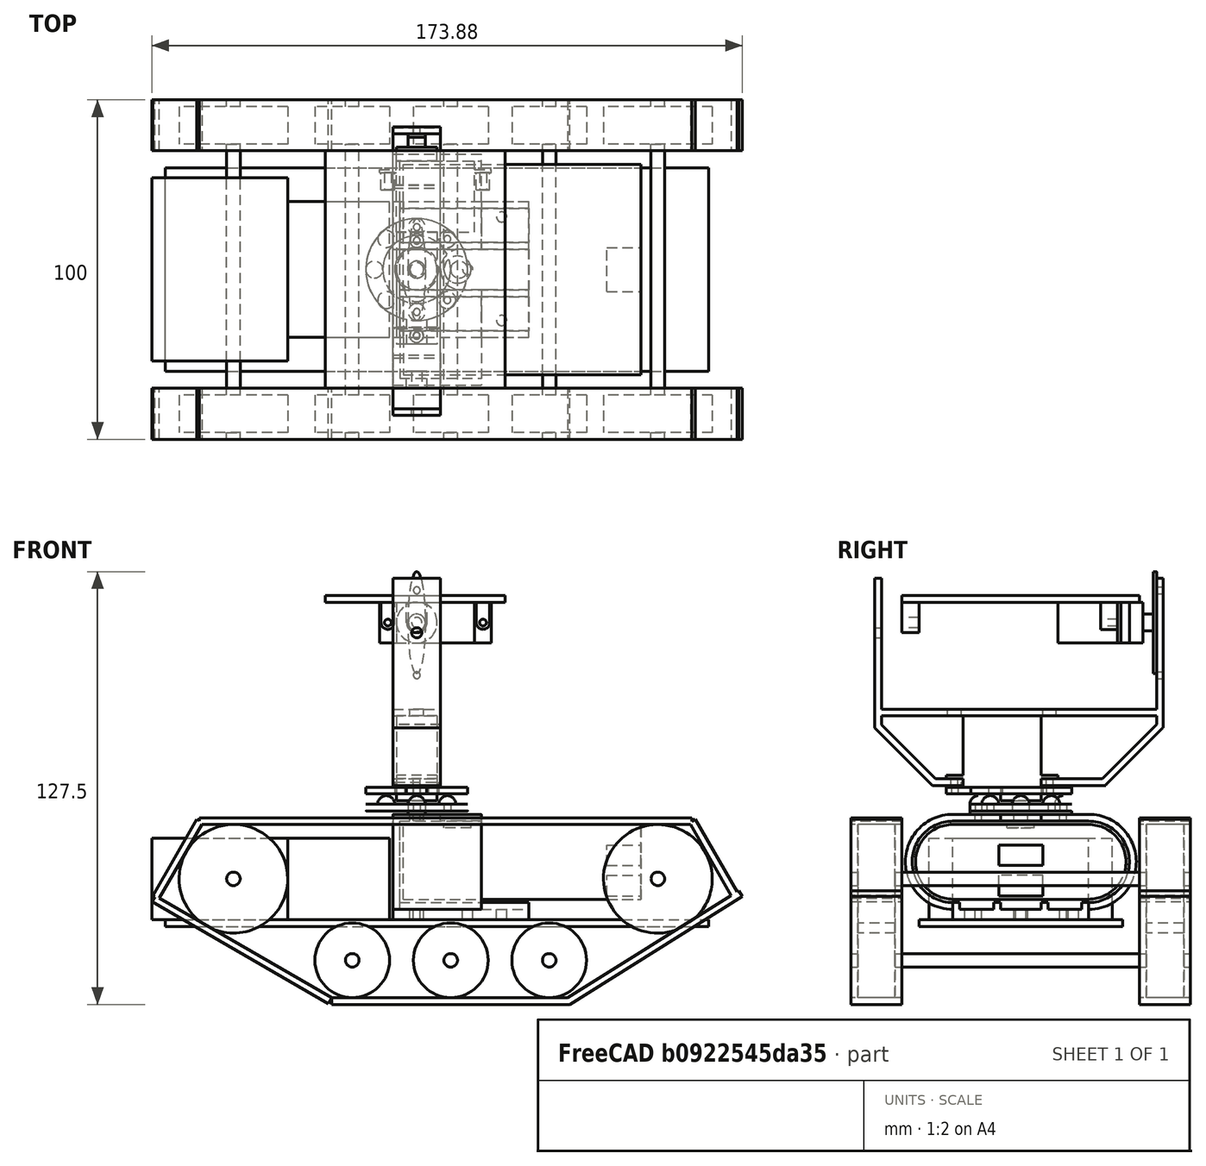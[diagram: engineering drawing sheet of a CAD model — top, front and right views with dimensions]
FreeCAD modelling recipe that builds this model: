
FCSTD DOCUMENT
Label: androidtank_6
License: CC-BY 3.0
LicenseURL: http://creativecommons.org/licenses/by/3.0/
objects: Part::Cylinder×51, Part::Box×36, Part::MultiFuse×25, Part::Sphere×8, Part::Cut×7, Part::FeaturePython×1, App::DocumentObjectGroup×1
note: 128 computed .brp shape members not serialized (recipe doc carries the construction recipe); baked Part::Feature solids carry a one-line shape summary decoded from their .brp

FEATURE [Part::Box] Box  label="MainFrame"
  Height = 2
  Length = 160
  Width = 60
FEATURE [Part::Box] Box001001  label="Moter Unit2"
  Height = 24
  Length = 30
  Placement = pos=(36,10,2) rot=(0,0,1;0rad)
  Width = 40
FEATURE [Part::Cylinder] Cylinder  label="Shaft"
  Angle = 360
  Height = 100
  Placement = pos=(20,-20,14) rot=(-1,0,0;1.5708rad)
  Radius = 2
FEATURE [Part::Box] Box001002
  Height = 2
  Length = 145
  Placement = pos=(10,-20,30) rot=(0,0,1;0rad)
  Width = 15
FEATURE [Part::Box] Box001002001
  Height = 2
  Length = 70
  Placement = pos=(49,-20,-23) rot=(0,0,1;0rad)
  Width = 15
FEATURE [Part::Box] Box001002001001
  Height = 2
  Length = 60
  Placement = pos=(119,-20,-23) rot=(0,-1,0;0.558505rad)
  Width = 15
FEATURE [Part::Box] Box001002001002
  Height = 2
  Length = 60
  Placement = pos=(49,-20,-21) rot=(0,1,0;3.66519rad)
  Width = 15
FEATURE [Part::Box] Box001002001003
  Height = 2
  Length = 26
  Placement = pos=(-2,-20,8) rot=(0,-1,0;1.0472rad)
  Width = 15
FEATURE [Part::Box] Box001002001003001
  Height = 2
  Length = 26
  Placement = pos=(169,-20,9) rot=(0,-1,0;2.0944rad)
  Width = 15
FEATURE [Part::MultiFuse] Fusion002001002  label="Caterpiller1"
  Shapes = -> [Box001002,Box001002001,Box001002001002,Box001002001001,Box001002001003,Box001002001003001]
FEATURE [Part::MultiFuse] Fusion002001002001  label="Caterpiller2"
  Placement = pos=(0,85,0) rot=(0,0,1;0rad)
  Shapes = -> [Box001002,Box001002001,Box001002001002,Box001002001001,Box001002001003,Box001002001003001]
FEATURE [Part::Cylinder] Cylinder002001001002  label="Wheel006"
  Angle = 360
  Height = 11
  Placement = pos=(20,78,14) rot=(1,0,0;1.5708rad)
  Radius = 11
FEATURE [Part::Cylinder] Cylinder002001001002001  label="Wheel007"
  Angle = 360
  Height = 11
  Placement = pos=(20,-7,14) rot=(1,0,0;1.5708rad)
  Radius = 11
FEATURE [Part::Cylinder] Cylinder002001002001  label="Shaft002"
  Angle = 360
  Height = 100
  Placement = pos=(20,-20,14) rot=(-1,0,0;1.5708rad)
  Radius = 2
FEATURE [Part::MultiFuse] Fusion002001002002002  label="SWheelSet1"
  Placement = pos=(35,0,-24) rot=(0,0,1;0rad)
  Shapes = -> [Cylinder002001002001,Cylinder002001001002,Cylinder002001001002001]
FEATURE [Part::MultiFuse] Fusion002001002002002001  label="SWheelSet2"
  Placement = pos=(64,0,-24) rot=(0,0,1;0rad)
  Shapes = -> [Cylinder002001002001,Cylinder002001001002,Cylinder002001001002001]
FEATURE [Part::MultiFuse] Fusion002001002002002001001  label="SWheelSet3"
  Placement = pos=(93,0,-24) rot=(0,0,1;0rad)
  Shapes = -> [Cylinder002001002001,Cylinder002001001002,Cylinder002001001002001]
FEATURE [Part::Box] Box001002001003002
  Height = 22
  Length = 70
  Placement = pos=(0,0,-11) rot=(0,0,1;0rad)
  Width = 40
FEATURE [Part::Cylinder] Cylinder002001001002002
  Angle = 360
  Height = 70
  Placement = pos=(0,0,0) rot=(0,1,0;1.5708rad)
  Radius = 11
FEATURE [Part::Cylinder] Cylinder001
  Angle = 360
  Height = 70
  Placement = pos=(0,40,0) rot=(0,1,0;1.5708rad)
  Radius = 11
FEATURE [Part::Cylinder] Cylinder002001001002003  label="PowerButton"
  Angle = 360
  Height = 2
  Placement = pos=(16,20,10) rot=(0,0,1;0rad)
  Radius = 4
FEATURE [Part::Box] Box001002001003003  label="USB1"
  Height = 6
  Length = 15
  Placement = pos=(60,13.5,-1) rot=(0,0,1;0rad)
  Width = 13
FEATURE [Part::Box] Box001001001  label="USB2"
  Height = 6
  Length = 15
  Placement = pos=(60,13.5,-10) rot=(0,0,1;0rad)
  Width = 13
FEATURE [Part::MultiFuse] Fusion002001002002002001002
  Shapes = -> [Cylinder001,Box001002001003002,Cylinder002001001002002]
FEATURE [Part::MultiFuse] Fusion001001
  Shapes = -> [Box001001001,Cylinder002001001002003,Box001002001003003]
FEATURE [Part::Cut] Cut  label="Eneloop"
  Base = -> Fusion002001002002002001002
  Placement = pos=(70,10,19) rot=(0,0,1;0rad)
  Tool = -> Fusion001001
FEATURE [Part::Cylinder] Cylinder001001  label="Cylinder002"
  Angle = 360
  Height = 26
  Placement = pos=(0,50,19) rot=(0,1,0;1.5708rad)
  Radius = 14
FEATURE [Part::Box] Box001002001003002001  label="Box001002001003002001001001001006001001002001003001006"
  Height = 28
  Length = 26
  Placement = pos=(0,10,5) rot=(0,0,1;0rad)
  Width = 40
FEATURE [Part::Cylinder] Cylinder002001001002002001  label="Cylinder003"
  Angle = 360
  Height = 26
  Placement = pos=(0,10,19) rot=(0,1,0;1.5708rad)
  Radius = 14
FEATURE [Part::Box] Box001  label="Moter Unit1"
  Height = 24
  Length = 40
  Placement = pos=(-4,3,2) rot=(0,0,1;0rad)
  Width = 54
FEATURE [Part::Box] Box001002001003002001001  label="Box003"
  Height = 5
  Length = 40
  Placement = pos=(0,10,2) rot=(0,0,1;0rad)
  Width = 40
FEATURE [Part::Box] Box001002001003002001002  label="Box004"
  Height = 24
  Length = 26
  Placement = pos=(2,10,7) rot=(0,0,1;0rad)
  Width = 40
FEATURE [Part::Cylinder] Cylinder001001001  label="Cylinder004"
  Angle = 360
  Height = 26
  Placement = pos=(2,50,19) rot=(0,1,0;1.5708rad)
  Radius = 12
FEATURE [Part::Cylinder] Cylinder002001001002002001001  label="Cylinder005"
  Angle = 360
  Height = 26
  Placement = pos=(2,10,19) rot=(0,1,0;1.5708rad)
  Radius = 12
FEATURE [Part::Cylinder] Cylinder002001001002003001  label="PowerButton001"
  Angle = 360
  Height = 4
  Placement = pos=(20,30,30) rot=(0,0,1;0rad)
  Radius = 6
FEATURE [Part::Box] Box001002001003002001003  label="Box005"
  Height = 4
  Length = 10
  Placement = pos=(20,24,30) rot=(0,0,1;0rad)
  Width = 12
FEATURE [Part::Box] Box001002001003002001001001  label="Box006"
  Height = 3
  Length = 40
  Placement = pos=(2,12,5) rot=(0,0,1;0rad)
  Width = 10
FEATURE [Part::Box] Box001002001003002001001001001  label="Box007"
  Height = 3
  Length = 40
  Placement = pos=(2,24,5) rot=(0,0,1;0rad)
  Width = 12
FEATURE [Part::Box] Box001002001003002001001001001001  label="Box008"
  Height = 3
  Length = 40
  Placement = pos=(2,38,5) rot=(0,0,1;0rad)
  Width = 10
FEATURE [Part::MultiFuse] Fusion002001002002002001003
  Shapes = -> [Box001002001003002001,Cylinder001001,Cylinder002001001002002001,Box001002001003002001001]
FEATURE [Part::MultiFuse] Fusion002001002002002001004
  Shapes = -> [Box001002001003002001002,Cylinder002001001002002001001,Cylinder001001001,Box001002001003002001001001001001,Box001002001003002001001001001,Box001002001003002001001001,Box001002001003002001003,Cylinder002001001002003001]
FEATURE [Part::Cut] Cut001  label="BatteryFrame"
  Base = -> Fusion002001002002002001003
  Placement = pos=(67,0,0) rot=(0,0,1;0rad)
  Tool = -> Fusion002001002002002001004
FEATURE [Part::Cylinder] Cylinder002001001002002001002001  label="Cylinder007"
  Angle = 360
  Height = 40
  Placement = pos=(74,17.5,0) rot=(0,0,1;0rad)
  Radius = 1
FEATURE [Part::Cylinder] Cylinder002001001002002001002  label="Cylinder006"
  Angle = 360
  Height = 40
  Placement = pos=(74,42.5,0) rot=(0,0,1;0rad)
  Radius = 1
FEATURE [Part::Cylinder] Cylinder002001001002002001002001001  label="Cylinder008"
  Angle = 360
  Height = 40
  Placement = pos=(89,30,0) rot=(0,0,1;0rad)
  Radius = 1.5
FEATURE [Part::Cylinder] Cylinder002001001002002001002001002  label="Cylinder009"
  Angle = 360
  Height = 40
  Placement = pos=(99,45.5,0) rot=(0,0,1;0rad)
  Radius = 1.5
FEATURE [Part::Cylinder] Cylinder002001001002002001002001003  label="Cylinder0010"
  Angle = 360
  Height = 40
  Placement = pos=(99,15,0) rot=(0,0,1;0rad)
  Radius = 1.5
FEATURE [Part::Box] Box001002001003002001001001001006  label="Box009"
  Height = 2
  Length = 53
  Placement = pos=(47,-5,100) rot=(0,0,1;0rad)
  Width = 70
FEATURE [Part::Box] Box001002001003002001001001001006001  label="Box010"
  Height = 44
  Length = 14
  Placement = pos=(67,70,66) rot=(0,0,1;0rad)
  Width = 2
FEATURE [Part::Box] Box001002001003002001001001001006001001  label="Box011"
  Height = 2
  Length = 13
  Placement = pos=(67.5,12.5,48) rot=(0,0,1;0rad)
  Width = 23.5
FEATURE [Part::Box] Box001002001003002001001001001006001001001  label="Box012"
  Height = 44
  Length = 14
  Placement = pos=(67,-13,66) rot=(0,0,1;0rad)
  Width = 2
FEATURE [Part::Cylinder] Cylinder002001001002002001002001008  label="Hole1"
  Angle = 360
  Height = 20
  Placement = pos=(74,-20,94) rot=(-1,0,0;1.5708rad)
  Radius = 1.5
FEATURE [Part::Cylinder] Cylinder002001001002002001002001008001  label="Hole2"
  Angle = 360
  Height = 20
  Placement = pos=(74,60,106.5) rot=(-1,0,0;1.5708rad)
  Radius = 1
FEATURE [Part::Cylinder] Cylinder002001001002002001002001008001001  label="Hole4"
  Angle = 360
  Height = 20
  Placement = pos=(74,38.5,41) rot=(0,0,1;0rad)
  Radius = 1
FEATURE [Part::Cylinder] Cylinder002001001002002001002001008001001001  label="Hole3"
  Angle = 360
  Height = 20
  Placement = pos=(74,60,81.5) rot=(-1,0,0;1.5708rad)
  Radius = 1
FEATURE [Part::Cylinder] Cylinder002001001002002001002001008001001002  label="Hole5"
  Angle = 360
  Height = 20
  Placement = pos=(74,10.5,41) rot=(0,0,1;0rad)
  Radius = 1
FEATURE [Part::Box] Box001002001003002001001001001006001001001001  label="Box013"
  Height = 24
  Length = 14
  Placement = pos=(67,4,49) rot=(1,0,0;0.785397rad)
  Width = 2
FEATURE [Part::Box] Box001002001003002001001001001006001001001001001  label="Box014"
  Height = 24
  Length = 14
  Placement = pos=(67,53.41,50.41) rot=(-1,0,0;0.785397rad)
  Width = 2
FEATURE [Part::Box] Box001002001003002001001001001006001001002001  label="Box016"
  Height = 2
  Length = 14
  Placement = pos=(67,4,49) rot=(0,0,1;0rad)
  Width = 9
FEATURE [Part::Box] Box001002001003002001001001001006001001002001001  label="Box017"
  Height = 2
  Length = 14
  Placement = pos=(67,36,49) rot=(0,0,1;0rad)
  Width = 19
FEATURE [Part::Box] Box001002001003002001001001001006001001002001002  label="Box015"
  Height = 2
  Length = 14
  Placement = pos=(67,-13,69.5) rot=(0,0,1;0rad)
  Width = 85
FEATURE [Part::MultiFuse] Fusion002001002002002001009
  Shapes = -> [Box001002001003002001001001001006001,Box001002001003002001001001001006001001001001,Box001002001003002001001001001006001001001,Box001002001003002001001001001006001001001001001,Box001002001003002001001001001006001001002001,Box001002001003002001001001001006001001002001002,Box001002001003002001001001001006001001002001001]
FEATURE [Part::Cylinder] Cylinder002001001002002001002001008001001002001  label="Hole006"
  Angle = 360
  Height = 20
  Placement = pos=(74,10.5,60) rot=(0,0,1;0rad)
  Radius = 2
FEATURE [Part::Cylinder] Cylinder002001001002002001002001008001001002002  label="Hole007"
  Angle = 360
  Height = 20
  Placement = pos=(74,38.5,60) rot=(0,0,1;0rad)
  Radius = 2
FEATURE [Part::MultiFuse] Fusion002001002002002001010
  Shapes = -> [Cylinder002001001002002001002001008001,Box001002001003002001001001001006001001,Cylinder002001001002002001002001008001001,Cylinder002001001002002001002001008,Cylinder002001001002002001002001008001001001,Cylinder002001001002002001002001008001001002,Cylinder002001001002002001002001008001001002002,Cylinder002001001002002001002001008001001002001]
FEATURE [Part::Cut] Cut003  label="HeadFrame"
  Base = -> Fusion002001002002002001009
  Placement = pos=(0,0,-7.5) rot=(0,0,1;0rad)
  Tool = -> Fusion002001002002002001010
FEATURE [Part::Cylinder] Cylinder002001001002002001002001008001001002003  label="Cylinder025"
  Angle = 360
  Height = 5
  Placement = pos=(74,0,94) rot=(1,0,0;1.5708rad)
  Radius = 3
FEATURE [Part::Box] Box001002001003002001001001001006001001002001003  label="Box020"
  Height = 6
  Length = 6
  Placement = pos=(71,-5,94) rot=(0,0,1;0rad)
  Width = 5
FEATURE [Part::Cylinder] Cylinder002001001002002001002001008001001002003001  label="Cylinder026"
  Angle = 360
  Height = 7
  Placement = pos=(74,1,94) rot=(1,0,0;1.5708rad)
  Radius = 1.5
FEATURE [Part::Box] Box001002001003002001001001001006001001002001003001001  label="Box022"
  Height = 6
  Length = 4
  Placement = pos=(91.5,53.5,94) rot=(0,0,1;0rad)
  Width = 5
FEATURE [Part::Cylinder] Cylinder002001001002002001002001008001001002003002  label="Cylinder027"
  Angle = 360
  Height = 5
  Placement = pos=(65.5,58.5,94) rot=(1,0,0;1.5708rad)
  Radius = 2
FEATURE [Part::Cylinder] Cylinder002001001002002001002001008001001002003002001  label="Cylinder028"
  Angle = 360
  Height = 5
  Placement = pos=(93.5,58.5,94) rot=(1,0,0;1.5708rad)
  Radius = 2
FEATURE [Part::Box] Box001002001003002001001001001006001001002001003001  label="Box021"
  Height = 6
  Length = 4
  Placement = pos=(63.5,53.5,94) rot=(0,0,1;0rad)
  Width = 5
FEATURE [Part::Cylinder] Cylinder002001001002002001002001008001001002003002002  label="Cylinder029"
  Angle = 360
  Height = 6
  Placement = pos=(65.5,59,94) rot=(1,0,0;1.5708rad)
  Radius = 1
FEATURE [Part::Cylinder] Cylinder002001001002002001002001008001001002003002001001  label="Cylinder030"
  Angle = 360
  Height = 6
  Placement = pos=(93.5,59,94) rot=(1,0,0;1.5708rad)
  Radius = 1
FEATURE [Part::MultiFuse] Fusion002001002002002001011
  Shapes = -> [Box001002001003002001001001001006,Box001002001003002001001001001006001001002001003001001,Cylinder002001001002002001002001008001001002003002001,Box001002001003002001001001001006001001002001003,Cylinder002001001002002001002001008001001002003,Box001002001003002001001001001006001001002001003001,Cylinder002001001002002001002001008001001002003002]
FEATURE [Part::MultiFuse] Fusion002001002002002001012
  Shapes = -> [Cylinder002001001002002001002001008001001002003001,Cylinder002001001002002001002001008001001002003002002,Cylinder002001001002002001002001008001001002003002001001]
FEATURE [Part::Cut] Cut002003  label="HeadMount"
  Base = -> Fusion002001002002002001011
  Placement = pos=(0,0,-4.5) rot=(0,0,1;0rad)
  Tool = -> Fusion002001002002002001012
FEATURE [Part::Cylinder] Cylinder002001001002002001002001001001  label="Cylinder040"
  Angle = 360
  Height = 40
  Placement = pos=(74,30,0) rot=(0,0,1;0rad)
  Radius = 2
FEATURE [Part::MultiFuse] Fusion002001002002002001013  label="BatteryFrameHoles"
  Shapes = -> [Cylinder002001001002002001002001,Cylinder002001001002002001002,Cylinder002001001002002001002001001,Cylinder002001001002002001002001002,Cylinder002001001002002001002001003,Cylinder002001001002002001002001001001]
FEATURE [Part::Cut] Cut002004  label="BatteryFrame2"
  Base = -> Cut001
  Tool = -> Fusion002001002002002001013
FEATURE [Part::Box] Box001002001003002001001001001006001001002001003001002  label="ServoBody"
  Height = 21
  Length = 23
  Width = 12
FEATURE [Part::Cylinder] Cylinder002001001002002001002001008001001002003002001002  label="ServoBody2"
  Angle = 360
  Height = 4
  Placement = pos=(6,6,21) rot=(0,0,1;0rad)
  Radius = 6
FEATURE [Part::Box] Box001002001003002001001001001006001001002001003001003  label="ServoBody3"
  Height = 1
  Length = 33
  Placement = pos=(-5,0,17.5) rot=(0,0,1;0rad)
  Width = 12
FEATURE [Part::Cylinder] Cylinder001001002  label="ServoAxis"
  Angle = 360
  Height = 4
  Placement = pos=(6,6,24) rot=(0,0,1;0rad)
  Radius = 2.5
FEATURE [Part::MultiFuse] Fusion005  label="ServoArmL"
  Shapes = -> [Cylinder001001002,Box001002001003002001001001001006001001002001003001003,Box001002001003002001001001001006001001002001003001002,Cylinder002001001002002001002001008001001002003002001002]
FEATURE [Part::MultiFuse] Fusion006  label="ServoYaw"
  Placement = pos=(80,36,62) rot=(0.707107,-0.707107,0;3.14159rad)
  Shapes = -> [Fusion005]
FEATURE [Part::Cylinder] Cylinder003001001003002  label="Cylinder002001001002002001002001008001001002003002001005002"
  Angle = 360
  Height = 2
  Placement = pos=(6,6,26) rot=(0,0,1;0rad)
  Radius = 15
FEATURE [Part::Cylinder] Cylinder003001001004  label="Cylinder002001001002002001002001008001001002003002001006"
  Angle = 360
  Height = 0.5
  Placement = pos=(-2.5,6,20.5) rot=(0,0,1;0rad)
  Radius = 2
FEATURE [Part::Cylinder] Cylinder003001001005  label="Cylinder011"
  Angle = 360
  Height = 2
  Placement = pos=(6,6,21) rot=(0,0,1;0rad)
  Radius = 15
FEATURE [Part::Cylinder] Cylinder003001001004001  label="Cylinder010"
  Angle = 360
  Height = 0.5
  Placement = pos=(25.5,6,20.5) rot=(0,0,1;0rad)
  Radius = 2
FEATURE [Part::Cylinder] Cylinder003001001005001  label="Cylinder012"
  Angle = 360
  Height = 2
  Placement = pos=(6,6,21) rot=(0,0,1;0rad)
  Radius = 6.5
FEATURE [Part::Cylinder] Cylinder003001001005001001  label="Cylinder013"
  Angle = 360
  Height = 2
  Placement = pos=(12,6,21) rot=(0,0,1;0rad)
  Radius = 3.5
FEATURE [Part::Box] Box002
  Height = 2
  Length = 10
  Placement = pos=(18,3,21) rot=(0,0,1;0rad)
  Width = 6
FEATURE [Part::Cylinder] Cylinder003001001004002  label="Cylinder014"
  Angle = 360
  Height = 5
  Placement = pos=(-2.5,6,19.5) rot=(0,0,1;0rad)
  Radius = 1
FEATURE [Part::Cylinder] Cylinder003001001004001001  label="Cylinder015"
  Angle = 360
  Height = 5
  Placement = pos=(25.5,6,19.5) rot=(0,0,1;0rad)
  Radius = 1
FEATURE [Part::MultiFuse] Fusion008
  Shapes = -> [Cylinder003001001005,Box002,Cylinder003001001004,Cylinder003001001004001]
FEATURE [Part::MultiFuse] Fusion009
  Shapes = -> [Cylinder003001001005001,Cylinder003001001005001001,Cylinder003001001004002,Cylinder003001001004001001]
FEATURE [Part::Cut] Cut002  label="Guide1"
  Base = -> Fusion008
  Placement = pos=(80,36,62) rot=(-0.705662,0.708549,0;3.14159rad)
  Tool = -> Fusion009
FEATURE [Part::Sphere] Sphere001001001001001001002
  Angle1 = -90
  Angle2 = 0
  Angle3 = 360
  Placement = pos=(-3,-3,26) rot=(0,0,1;0rad)
  Radius = 2.5
FEATURE [Part::Sphere] Sphere001001001001001001003
  Angle1 = -90
  Angle2 = 0
  Angle3 = 360
  Placement = pos=(15,-3,26) rot=(0,0,1;0rad)
  Radius = 2.5
FEATURE [Part::Sphere] Sphere001001001001001001004  label="Sphere001001001001001001001002"
  Angle1 = -90
  Angle2 = 0
  Angle3 = 360
  Placement = pos=(15,15,26) rot=(0,0,1;0rad)
  Radius = 2.5
FEATURE [Part::Sphere] Sphere001001001001001001005  label="Sphere001001001001001001001003"
  Angle1 = -90
  Angle2 = 0
  Angle3 = 360
  Placement = pos=(-3,15,26) rot=(0,0,1;0rad)
  Radius = 2.5
FEATURE [Part::Cylinder] Cylinder003001001005001004001  label="Cylinder002001001002002001002001008001001002003002001007"
  Angle = 360
  Height = 4
  Placement = pos=(-6.5,6,26) rot=(0,0,1;0rad)
  Radius = 1
FEATURE [Part::Cylinder] Cylinder003001001001003001  label="Cylinder002001001002002001002001008001001002003002001008"
  Angle = 360
  Height = 4
  Placement = pos=(18.5,6,26) rot=(0,0,1;0rad)
  Radius = 1
FEATURE [Part::Cylinder] Cylinder003001001005001003001001  label="Cylinder002001001002002001002001008001001002003002001009"
  Angle = 360
  Height = 5
  Placement = pos=(-3,-3,26) rot=(0,0,1;0rad)
  Radius = 1
FEATURE [Part::Cylinder] Cylinder003001001001002001001  label="Cylinder002001001002002001002001008001001002003002001010"
  Angle = 360
  Height = 5
  Placement = pos=(15,-3,26) rot=(0,0,1;0rad)
  Radius = 1
FEATURE [Part::Sphere] Sphere001001001001001001006  label="Sphere001001001001001001001004"
  Angle1 = -90
  Angle2 = 0
  Angle3 = 360
  Placement = pos=(-6.5,6,26) rot=(0,0,1;0rad)
  Radius = 2.5
FEATURE [Part::Sphere] Sphere001001001001001001007  label="Sphere001001001001001001001005"
  Angle1 = -90
  Angle2 = 0
  Angle3 = 360
  Placement = pos=(18.5,6,26) rot=(0,0,1;0rad)
  Radius = 2.5
FEATURE [Part::Sphere] Sphere001001001001001001008  label="Sphere001001001001001001001006"
  Angle1 = -90
  Angle2 = 0
  Angle3 = 360
  Placement = pos=(6,-6.5,26) rot=(0,0,1;0rad)
  Radius = 2.5
FEATURE [Part::Sphere] Sphere001001001001001001001001  label="Sphere001001001001001001001007"
  Angle1 = -90
  Angle2 = 0
  Angle3 = 360
  Placement = pos=(6,18.5,26) rot=(0,0,1;0rad)
  Radius = 2.5
FEATURE [Part::Cylinder] Cylinder003001001003001001  label="Cylinder002001001002002001002001008001001002003002001011"
  Angle = 360
  Height = 2
  Placement = pos=(6,6,26) rot=(0,0,1;0rad)
  Radius = 10
FEATURE [Part::MultiFuse] Fusion013001
  Shapes = -> [Cylinder003001001003001001,Cylinder003001001005001003001001,Cylinder003001001001002001001,Cylinder003001001005001004001,Cylinder003001001001003001]
FEATURE [Part::MultiFuse] Fusion014
  Shapes = -> [Sphere001001001001001001002,Cylinder003001001003002,Sphere001001001001001001005,Sphere001001001001001001008,Sphere001001001001001001006,Sphere001001001001001001003,Sphere001001001001001001004,Sphere001001001001001001001001,Sphere001001001001001001007]
FEATURE [Part::Cut] Cut002005  label="Guide2"
  Base = -> Fusion014
  Placement = pos=(80,36,62) rot=(0.707107,-0.707107,0;3.14159rad)
  Tool = -> Fusion013001
FEATURE [Part::Box] Box001002001003002001001001001006001001002001003001004  label="ServoBody004"
  Height = 21
  Length = 23
  Width = 12
FEATURE [Part::Cylinder] Cylinder002001001002002001002001008001001002003002001003  label="ServoBody005"
  Angle = 360
  Height = 4
  Placement = pos=(6,6,21) rot=(0,0,1;0rad)
  Radius = 6
FEATURE [Part::Box] Box001002001003002001001001001006001001002001003001005  label="ServoBody006"
  Height = 1
  Length = 33
  Placement = pos=(-5,0,17.5) rot=(0,0,1;0rad)
  Width = 12
FEATURE [Part::Cylinder] Cylinder001001003  label="ServoAxis001"
  Angle = 360
  Height = 4
  Placement = pos=(6,6,24) rot=(0,0,1;0rad)
  Radius = 2.5
FEATURE [Part::MultiFuse] Fusion005001  label="ServoArmL001"
  Shapes = -> [Cylinder001001003,Box001002001003002001001001001006001001002001003001005,Box001002001003002001001001001006001001002001003001004,Cylinder002001001002002001002001008001001002003002001003]
FEATURE [Part::Cylinder] Cylinder002001001002002001002001008001001002003002001004  label="Cylinder002001001002002001002001008001001002003002001012"
  Angle = 360
  Height = 2
  Radius = 2.5
FEATURE [Part::FeaturePython] Scale  # Draft clone (typed FeaturePython)
  Objects = -> [Cylinder002001001002002001002001008001001002003002001004]
  Placement = pos=(0,0,1) rot=(0,0,1;0rad)
  Scale = (6,1,0.5)
FEATURE [Part::MultiFuse] Fusion  label="Arm"
  Placement = pos=(6,6,27) rot=(0,0,1;1.5708rad)
  Shapes = -> [Cylinder002001001002002001002001008001001002003002001004,Scale]
FEATURE [Part::MultiFuse] Fusion006001  label="ServoPitch"
  Placement = pos=(68,41,95.5) rot=(-1,0,0;1.5708rad)
  Shapes = -> [Fusion005001,Fusion]
FEATURE [Part::Cylinder] Cylinder002001001002002001002001008001001002003002001005  label="Wheel1"
  Angle = 360
  Height = 11
  Placement = pos=(20,78,14) rot=(1,0,0;1.5708rad)
  Radius = 16
FEATURE [Part::Cylinder] Cylinder002001001002002001002001008001001002003002001005001  label="Wheel2"
  Angle = 360
  Height = 11
  Placement = pos=(20,-7,14) rot=(1,0,0;1.5708rad)
  Radius = 16
FEATURE [Part::MultiFuse] Fusion002001002002002001014  label="LWheelSet1"
  Shapes = -> [Cylinder,Cylinder002001001002002001002001008001001002003002001005,Cylinder002001001002002001002001008001001002003002001005001]
FEATURE [Part::MultiFuse] Fusion002001002002002001014001  label="LWheelSet2"
  Placement = pos=(125,0,0) rot=(0,0,1;0rad)
  Shapes = -> [Cylinder,Cylinder002001001002002001002001008001001002003002001005,Cylinder002001001002002001002001008001001002003002001005001]
FEATURE [App::DocumentObjectGroup] ____________  label="DriveFrame"
  Group = -> [Box,Box001,Box001001,Fusion002001002,Fusion002001002001,Fusion002001002002002,Fusion002001002002002001,Fusion002001002002002001001,Fusion002001002002002001014,Fusion002001002002002001014001]
